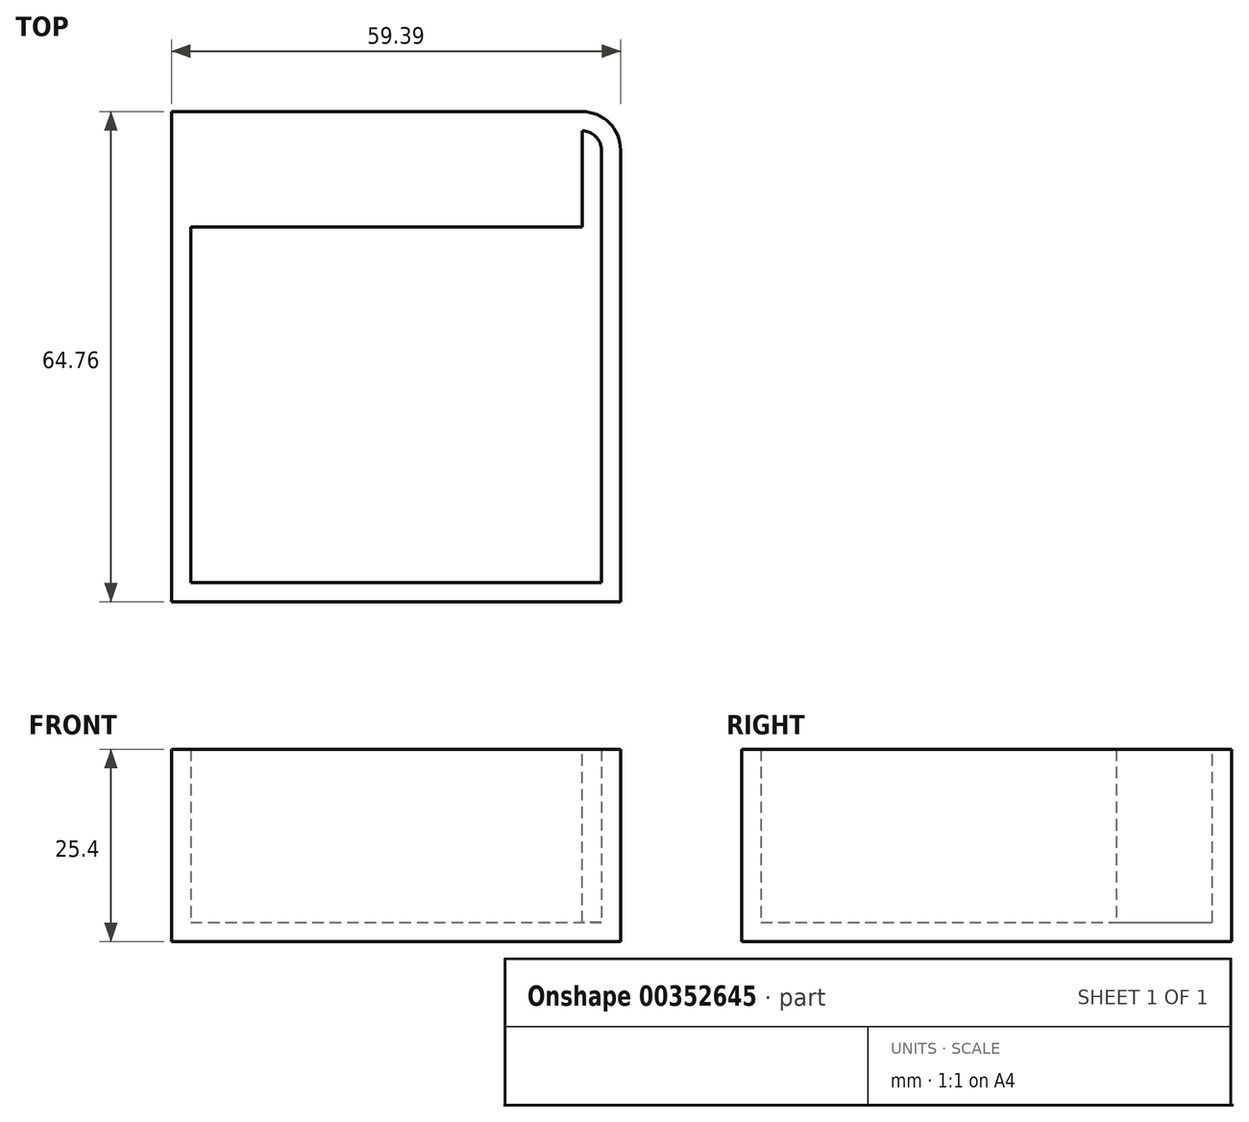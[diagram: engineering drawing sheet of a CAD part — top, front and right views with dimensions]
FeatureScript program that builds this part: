
annotation { "Feature Type Name" : "Feature", "Feature Type Description" : "" }
export const myFeature = defineFeature(function(context is Context, id is Id, definition is map)
    precondition{}
    {
        {
            var Q0;
            Q0=qCreatedBy(makeId("Top.planeOp"),FACE);
            var sketch = newSketch(context, id + "F0", { "sketchPlane" : qUnion([Q0])});
            skLineSegment(sketch, "E0.bottom", {"start": v(0, 0) * mm, "end": v(59.39, 0) * mm});
            skLineSegment(sketch, "E0.top", {"start": v(0, 64.76) * mm, "end": v(59.39, 64.76) * mm});
            skLineSegment(sketch, "E0.left", {"start": v(0, 0) * mm, "end": v(0, 64.76) * mm});
            skLineSegment(sketch, "E0.right", {"start": v(59.39, 0) * mm, "end": v(59.39, 64.76) * mm});
            skSolve(sketch);
        }
        {
            var Q0;
            Q0=makeQuery(id+"F0.imprint","IMPRINT",FACE,{"disambiguationData":[TD([[makeQuery(id+"F0.imprint","IMPRINT",EDGE,{"derivedFrom":sQuery(id+"F0.wireOp",EDGE,"E0.bottom")}),1.0]])]});
            extrude(context, id + "F1", {"entities" : qUnion([Q0]), "depth" : 25.4 * mm});
        }
        {
            var Q0;
            Q0=makeQuery(id+"F1.opExtrude","SWEPT_EDGE",EDGE,{"disambiguationData":[OSD([sQuery(id+"F0.wireOp",EDGE,"E0.top"),sQuery(id+"F0.wireOp",EDGE,"E0.right")])]});
            fillet(context, id + "F2", {"entities" : qUnion([Q0]), "radius" : 5.08 * mm, "tangentPropagation" : true, "allowEdgeOverflow" : false});
        }
        {
            var Q0;
            Q0=makeQuery(id+"F1.opExtrude","CAP_FACE",FACE,{"disambiguationData":[OSD([sQuery(id+"F0.wireOp",EDGE,"E0.bottom"),sQuery(id+"F0.wireOp",EDGE,"E0.top"),sQuery(id+"F0.wireOp",EDGE,"E0.left"),sQuery(id+"F0.wireOp",EDGE,"E0.right")])],"isStart":false});
            var sketch = newSketch(context, id + "F3", { "sketchPlane" : qUnion([Q0])});
            skLineSegment(sketch, "E1", {"start": v(28.72, 36.21) * mm, "end": v(49.28, 36.21) * mm});
            skLineSegment(sketch, "E2", {"start": v(49.28, 36.21) * mm, "end": v(48.55, 51.12) * mm});
            skLineSegment(sketch, "E3", {"start": v(48.55, 51.12) * mm, "end": v(26.85, 51.12) * mm});
            skLineSegment(sketch, "E4", {"start": v(26.85, 51.12) * mm, "end": v(28.72, 36.21) * mm});
            skSolve(sketch);
        }
        {
            var Q0;
            Q0 = qSketchRegion(id + "F3", true);
            extrude(context, id + "F4", {"entities" : qUnion([Q0]), "operationType" : NewBodyOperationType.ADD, "oppositeDirection" : true, "depth" : 25.4 * mm});
        }
        {
            var Q0;
            Q0=makeQuery(id+"F1.opExtrude","CAP_FACE",FACE,{"disambiguationData":[OSD([sQuery(id+"F0.wireOp",EDGE,"E0.bottom"),sQuery(id+"F0.wireOp",EDGE,"E0.top"),sQuery(id+"F0.wireOp",EDGE,"E0.left"),sQuery(id+"F0.wireOp",EDGE,"E0.right")])],"isStart":false});
            var Q1;
            Q1=makeQuery(id+"F1.opExtrude","SWEPT_BODY",BODY,{"disambiguationData":[OSD([sQuery(id+"F0.wireOp",EDGE,"E0.bottom"),sQuery(id+"F0.wireOp",EDGE,"E0.top"),sQuery(id+"F0.wireOp",EDGE,"E0.left"),sQuery(id+"F0.wireOp",EDGE,"E0.right")])]});
            shell(context, id + "F5", {"entities" : qUnion([Q0]), "parts" : qUnion([Q1]), "thickness" : 2.54 * mm});
        }
        {
            var Q0;
            Q0=makeQuery(id+"F5.opShell","OFFSET_FACE",FACE,{"disambiguationData":[OSD([sQuery(id+"F0.wireOp",EDGE,"E0.top")])]});
            extrude(context, id + "F6", {"entities" : qUnion([Q0]), "operationType" : NewBodyOperationType.ADD, "depth" : 12.7 * mm});
        }
    });
